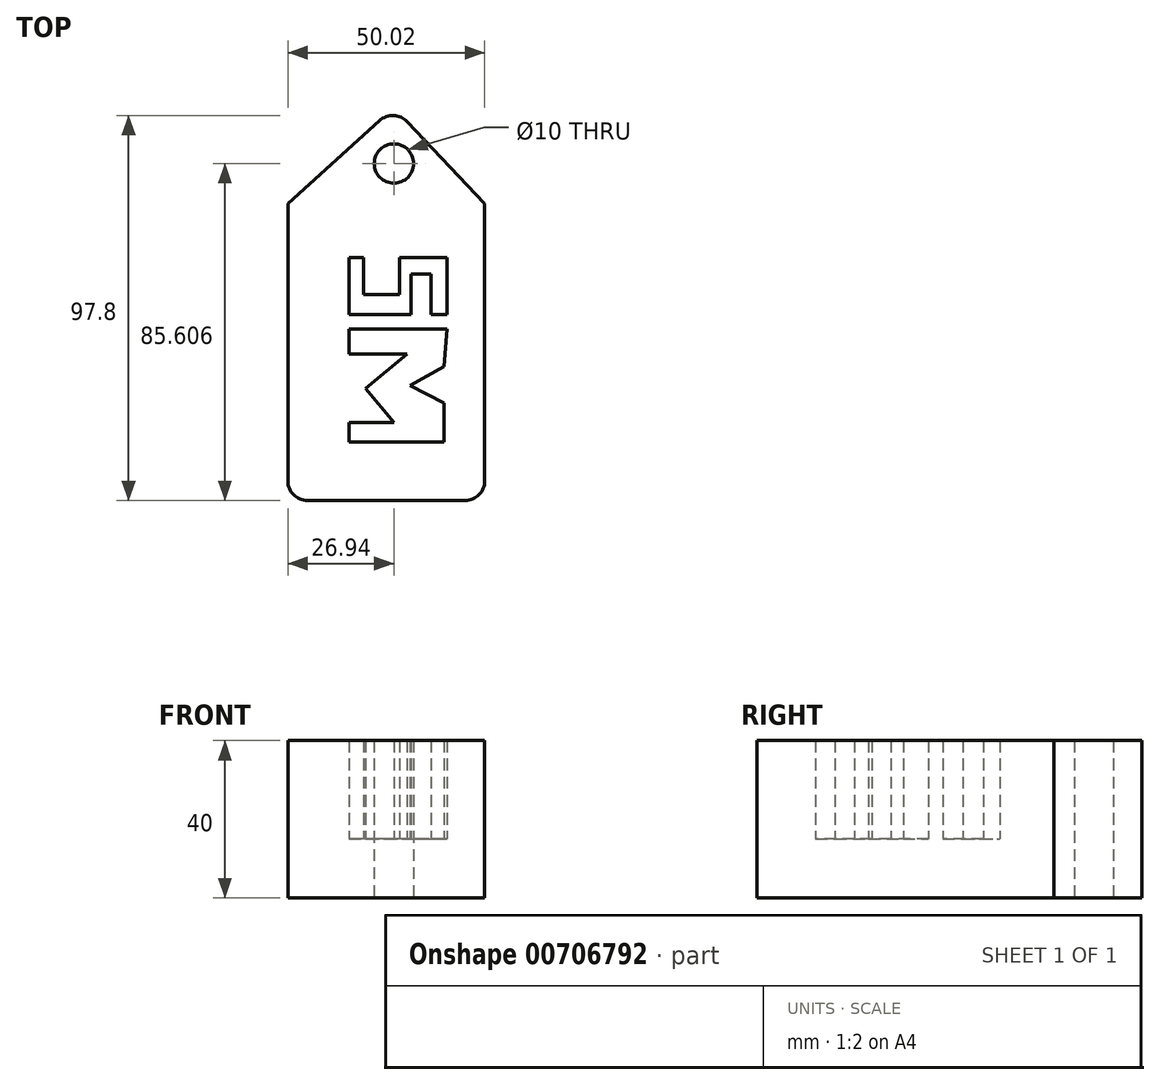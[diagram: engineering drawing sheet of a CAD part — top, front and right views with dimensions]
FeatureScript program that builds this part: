
annotation { "Feature Type Name" : "Feature", "Feature Type Description" : "" }
export const myFeature = defineFeature(function(context is Context, id is Id, definition is map)
    precondition{}
    {
        {
            var Q0;
            Q0=qCreatedBy(makeId("Top.planeOp"),FACE);
            var sketch = newSketch(context, id + "F0", { "sketchPlane" : qUnion([Q0])});
            skLineSegment(sketch, "E0", {"start": v(-21.94, -43.61) * mm, "end": v(18.08, -43.61) * mm});
            skLineSegment(sketch, "E1", {"start": v(23.08, -38.61) * mm, "end": v(23.08, 31.8) * mm});
            skLineSegment(sketch, "E2", {"start": v(23.08, 31.8) * mm, "end": v(-26.94, 31.8) * mm});
            skLineSegment(sketch, "E3", {"start": v(-26.94, 31.8) * mm, "end": v(-26.94, -38.61) * mm});
            skLineSegment(sketch, "E4", {"start": v(-26.94, 31.8) * mm, "end": v(-3.63, 52.9) * mm});
            skLineSegment(sketch, "E5", {"start": v(3.36, 52.63) * mm, "end": v(23.08, 31.8) * mm});
            skPoint(sketch, "E6.visualSharp", {"position": v(0, 56.18) * mm});
            skArc(sketch, "E6.filletArc", {"start": v(3.36, 52.63) * mm, "mid": v(-0.08, 54.19) * mm, "end": v(-3.63, 52.9) * mm});
            skPoint(sketch, "E7.visualSharp", {"position": v(-26.94, -43.61) * mm});
            skArc(sketch, "E7.filletArc", {"start": v(-26.94, -38.61) * mm, "mid": v(-25.48, -42.15) * mm, "end": v(-21.94, -43.61) * mm});
            skPoint(sketch, "E8.visualSharp", {"position": v(23.08, -43.61) * mm});
            skArc(sketch, "E8.filletArc", {"start": v(18.08, -43.61) * mm, "mid": v(21.62, -42.15) * mm, "end": v(23.08, -38.61) * mm});
            skSolve(sketch);
        }
        {
            var Q0;
            Q0 = qSketchRegion(id + "F0", true);
            extrude(context, id + "F1", {"entities" : qUnion([Q0]), "depth" : 15 * mm, "offsetDistance" : 25 * mm});
        }
        {
            var Q0;
            Q0=qCreatedBy(makeId("Top.planeOp"),FACE);
            var sketch = newSketch(context, id + "F2", { "sketchPlane" : qUnion([Q0])});
            skCircle(sketch, "E9", {"center": v(0, 42) * mm, "radius": 5.5 * mm});
            skSolve(sketch);
        }
        {
            var Q0;
            Q0=sQuery(id+"F2.wireOp",VERTEX,"E9.center");
            var Q1;
            Q1=makeQuery(id+"F1.opExtrude","SWEPT_BODY",BODY,{"disambiguationData":[OSD([sQuery(id+"F0.wireOp",EDGE,"E0"),sQuery(id+"F0.wireOp",EDGE,"E1"),sQuery(id+"F0.wireOp",EDGE,"E3"),sQuery(id+"F0.wireOp",EDGE,"E4"),sQuery(id+"F0.wireOp",EDGE,"E5"),sQuery(id+"F0.wireOp",EDGE,"E6.filletArc"),sQuery(id+"F0.wireOp",EDGE,"E7.filletArc"),sQuery(id+"F0.wireOp",EDGE,"E8.filletArc")])]});
            hole(context, id + "F3", {"style" : HoleStyle.SIMPLE, "endStyle" : HoleEndStyle.BLIND, "oppositeDirection" : true, "holeDiameter" : 10 * mm, "majorDiameter" : 5 * mm, "holeDepth" : 15 * mm, "isTappedThrough" : true, "tappedDepth" : 12 * mm, "tapClearance" : 3, "locations" : qUnion([Q0]), "scope" : qUnion([Q1])});
        }
        {
            var Q0;
            Q0=makeQuery(id+"F1.opExtrude","CAP_FACE",FACE,{"disambiguationData":[OSD([sQuery(id+"F0.wireOp",EDGE,"E0"),sQuery(id+"F0.wireOp",EDGE,"E1"),sQuery(id+"F0.wireOp",EDGE,"E3"),sQuery(id+"F0.wireOp",EDGE,"E4"),sQuery(id+"F0.wireOp",EDGE,"E5"),sQuery(id+"F0.wireOp",EDGE,"E6.filletArc"),sQuery(id+"F0.wireOp",EDGE,"E7.filletArc"),sQuery(id+"F0.wireOp",EDGE,"E8.filletArc")])],"isStart":false});
            var sketch = newSketch(context, id + "F4", { "sketchPlane" : qUnion([Q0])});
            skLineSegment(sketch, "E10", {"start": v(13.53, 11.7) * mm, "end": v(13.53, 18.06) * mm});
            skLineSegment(sketch, "E11", {"start": v(13.53, 18.06) * mm, "end": v(1.4, 18.06) * mm});
            skLineSegment(sketch, "E12", {"start": v(1.4, 18.06) * mm, "end": v(1.4, 8.76) * mm});
            skLineSegment(sketch, "E13", {"start": v(1.4, 8.76) * mm, "end": v(-7.65, 8.76) * mm});
            skLineSegment(sketch, "E14", {"start": v(-7.65, 8.76) * mm, "end": v(-7.65, 18.06) * mm});
            skLineSegment(sketch, "E15", {"start": v(-7.65, 18.06) * mm, "end": v(-11.33, 18.06) * mm});
            skLineSegment(sketch, "E16", {"start": v(-11.33, 18.06) * mm, "end": v(-11.33, 3.61) * mm});
            skLineSegment(sketch, "E17", {"start": v(-11.33, 3.61) * mm, "end": v(4.35, 3.61) * mm});
            skLineSegment(sketch, "E18", {"start": v(4.35, 3.61) * mm, "end": v(4.35, 13.9) * mm});
            skLineSegment(sketch, "E19", {"start": v(4.35, 13.9) * mm, "end": v(9.5, 13.9) * mm});
            skLineSegment(sketch, "E20", {"start": v(9.5, 13.9) * mm, "end": v(9.5, 3.61) * mm});
            skLineSegment(sketch, "E21", {"start": v(9.5, 3.61) * mm, "end": v(13.53, 3.61) * mm});
            skLineSegment(sketch, "E22", {"start": v(13.53, 3.61) * mm, "end": v(13.53, 11.7) * mm});
            skLineSegment(sketch, "E23", {"start": v(13.53, 0) * mm, "end": v(12.68, -9.61) * mm});
            skLineSegment(sketch, "E24", {"start": v(12.68, -9.61) * mm, "end": v(4.09, -14.43) * mm});
            skLineSegment(sketch, "E25", {"start": v(4.09, -14.43) * mm, "end": v(12.68, -18.87) * mm});
            skLineSegment(sketch, "E26", {"start": v(12.68, -18.87) * mm, "end": v(12.68, -28.72) * mm});
            skLineSegment(sketch, "E27", {"start": v(12.68, -28.72) * mm, "end": v(-11.33, -28.72) * mm});
            skLineSegment(sketch, "E28", {"start": v(-11.33, -28.72) * mm, "end": v(-11.33, -23.82) * mm});
            skLineSegment(sketch, "E29", {"start": v(-11.33, -23.82) * mm, "end": v(0, -23.82) * mm});
            skLineSegment(sketch, "E30", {"start": v(0, -23.82) * mm, "end": v(-7.17, -15.23) * mm});
            skLineSegment(sketch, "E31", {"start": v(-7.17, -15.23) * mm, "end": v(3.37, -6.43) * mm});
            skLineSegment(sketch, "E32", {"start": v(3.37, -6.43) * mm, "end": v(-11.33, -6.43) * mm});
            skLineSegment(sketch, "E33", {"start": v(-11.33, -6.43) * mm, "end": v(-11.33, 0) * mm});
            skLineSegment(sketch, "E34", {"start": v(-11.33, 0) * mm, "end": v(13.53, 0) * mm});
            skSolve(sketch);
        }
        {
            var Q0;
            Q0=makeQuery(id+"F4.imprint","IMPRINT",FACE,{"disambiguationData":[TD([[makeQuery(id+"F4.imprint","IMPRINT",EDGE,{"derivedFrom":sQuery(id+"F4.wireOp",EDGE,"E10")}),-1.0]])]});
            extrude(context, id + "F5", {"entities" : qUnion([Q0]), "operationType" : NewBodyOperationType.ADD, "depth" : 25 * mm, "offsetDistance" : 25 * mm});
        }
    });
